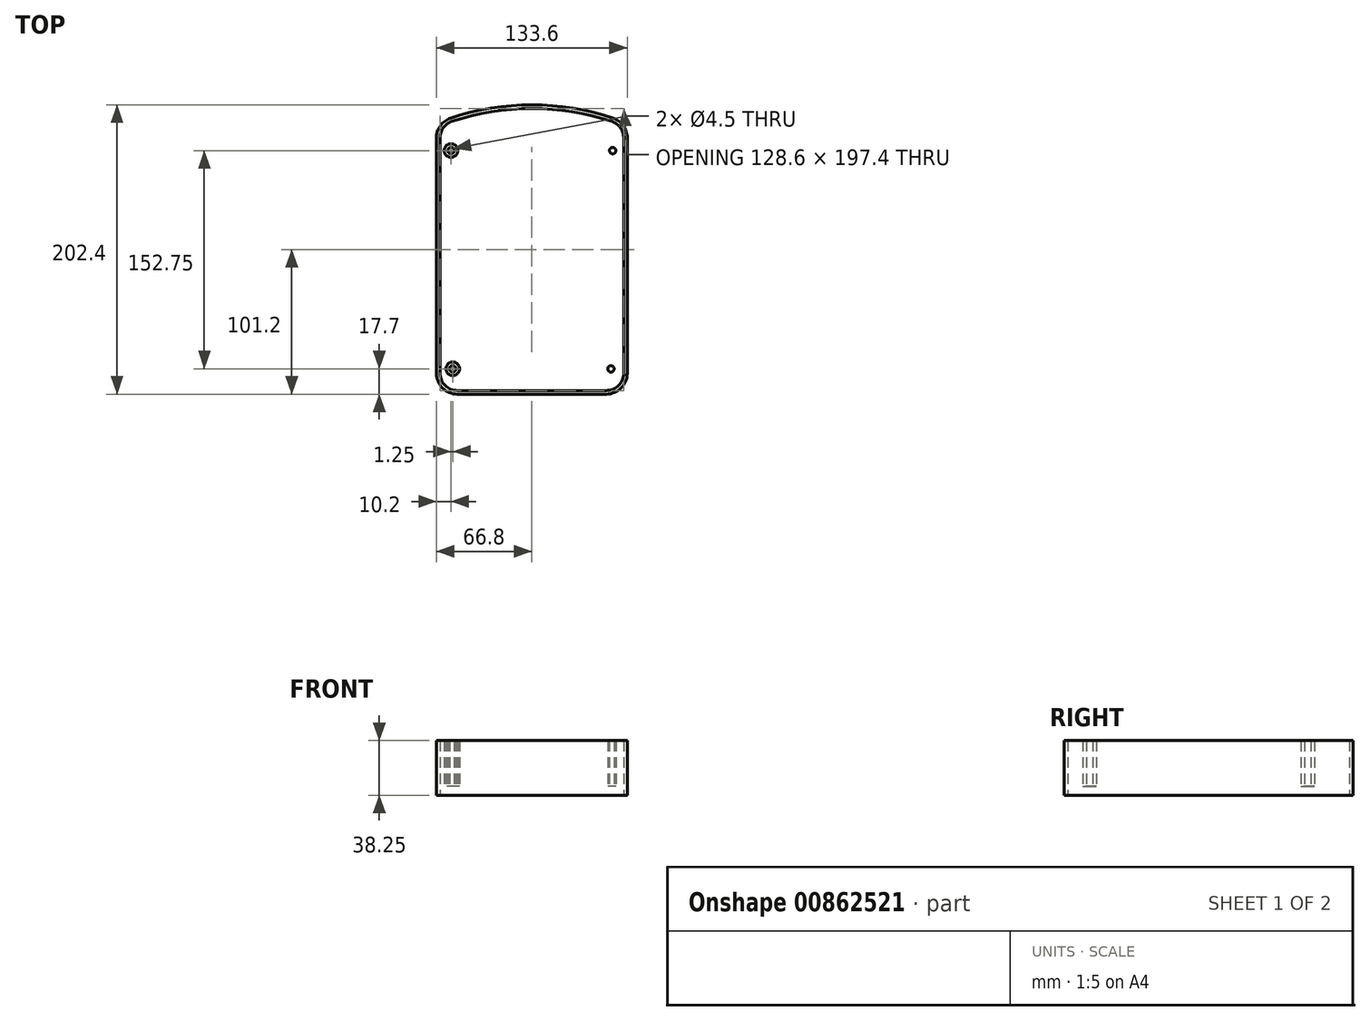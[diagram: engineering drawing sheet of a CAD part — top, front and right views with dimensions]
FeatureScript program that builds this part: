
annotation { "Feature Type Name" : "Feature", "Feature Type Description" : "" }
export const myFeature = defineFeature(function(context is Context, id is Id, definition is map)
    precondition{}
    {
        {
            var Q0;
            Q0=qCreatedBy(makeId("Top.planeOp"),FACE);
            var sketch = newSketch(context, id + "F0", { "sketchPlane" : qUnion([Q0])});
            skCircle(sketch, "E0", {"center": v(-55.35, -75) * mm, "radius": 2.25 * mm});
            skCircle(sketch, "E1", {"center": v(-56.6, 77.75) * mm, "radius": 2.25 * mm});
            skCircle(sketch, "E2.MirrorC", {"center": v(56.6, 77.75) * mm, "radius": 2.25 * mm});
            skCircle(sketch, "E3.MirrorC", {"center": v(55.35, -75) * mm, "radius": 2.25 * mm});
            skCircle(sketch, "E4", {"center": v(11.35, -59) * mm, "radius": 2.25 * mm});
            skLineSegment(sketch, "E5.bottom", {"start": v(-64.1, 95) * mm, "end": v(64.1, 95) * mm});
            skLineSegment(sketch, "E5.top", {"start": v(-52.1, -90) * mm, "end": v(52.1, -90) * mm});
            skLineSegment(sketch, "E5.left", {"start": v(-64.1, 86.57) * mm, "end": v(-64.1, -78) * mm});
            skLineSegment(sketch, "E5.right", {"start": v(64.1, 86.57) * mm, "end": v(64.1, -78) * mm});
            skPoint(sketch, "E5.middle", {"position": v(0, 2.5) * mm});
            skArc(sketch, "E6", {"start": v(55.88, 97.96) * mm, "mid": v(0, 107) * mm, "end": v(-55.88, 97.96) * mm});
            skPoint(sketch, "E7.visualSharp", {"position": v(-64.1, -90) * mm});
            skArc(sketch, "E7.filletArc", {"start": v(-64.1, -78) * mm, "mid": v(-60.59, -86.49) * mm, "end": v(-52.1, -90) * mm});
            skPoint(sketch, "E8.visualSharp", {"position": v(64.1, -90) * mm});
            skArc(sketch, "E8.filletArc", {"start": v(52.1, -90) * mm, "mid": v(60.59, -86.49) * mm, "end": v(64.1, -78) * mm});
            skPoint(sketch, "E9.visualSharp", {"position": v(-64.1, 95) * mm});
            skArc(sketch, "E9.filletArc", {"start": v(-55.88, 97.96) * mm, "mid": v(-61.83, 93.6) * mm, "end": v(-64.1, 86.57) * mm});
            skPoint(sketch, "E10.visualSharp", {"position": v(64.1, 95) * mm});
            skArc(sketch, "E10.filletArc", {"start": v(64.1, 86.57) * mm, "mid": v(61.83, 93.6) * mm, "end": v(55.88, 97.96) * mm});
            skCircle(sketch, "E11", {"center": v(56.6, 77.75) * mm, "radius": 4.75 * mm});
            skCircle(sketch, "E12", {"center": v(55.35, -75) * mm, "radius": 4.75 * mm});
            skCircle(sketch, "E13", {"center": v(-55.35, -75) * mm, "radius": 4.75 * mm});
            skCircle(sketch, "E14", {"center": v(-56.6, 77.75) * mm, "radius": 4.75 * mm});
            skLineSegment(sketch, "E15.0", {"start": v(-64.3, 86.57) * mm, "end": v(-64.3, -78) * mm});
            skLineSegment(sketch, "E16.0", {"start": v(64.3, 86.57) * mm, "end": v(64.3, -78) * mm});
            skArc(sketch, "E17.0", {"start": v(-64.3, -78) * mm, "mid": v(-60.73, -86.63) * mm, "end": v(-52.1, -90.2) * mm});
            skLineSegment(sketch, "E18.0", {"start": v(-52.1, -90.2) * mm, "end": v(52.1, -90.2) * mm});
            skArc(sketch, "E19.0", {"start": v(52.1, -90.2) * mm, "mid": v(60.73, -86.63) * mm, "end": v(64.3, -78) * mm});
            skArc(sketch, "E20.0", {"start": v(-55.95, 98.15) * mm, "mid": v(-62, 93.7) * mm, "end": v(-64.3, 86.57) * mm});
            skArc(sketch, "E21.0", {"start": v(55.95, 98.15) * mm, "mid": v(0, 107.2) * mm, "end": v(-55.95, 98.15) * mm});
            skArc(sketch, "E22.0", {"start": v(64.3, 86.57) * mm, "mid": v(62, 93.7) * mm, "end": v(55.95, 98.15) * mm});
            skArc(sketch, "E23.0", {"start": v(56.74, 100.52) * mm, "mid": v(0, 109.7) * mm, "end": v(-56.74, 100.52) * mm});
            skArc(sketch, "E24.0", {"start": v(-56.74, 100.52) * mm, "mid": v(-64.02, 95.17) * mm, "end": v(-66.8, 86.57) * mm});
            skLineSegment(sketch, "E25.0", {"start": v(-66.8, 86.57) * mm, "end": v(-66.8, -78) * mm});
            skArc(sketch, "E26.0", {"start": v(-66.8, -78) * mm, "mid": v(-62.5, -88.4) * mm, "end": v(-52.1, -92.7) * mm});
            skLineSegment(sketch, "E27.0", {"start": v(-52.1, -92.7) * mm, "end": v(52.1, -92.7) * mm});
            skArc(sketch, "E28.0", {"start": v(52.1, -92.7) * mm, "mid": v(62.5, -88.4) * mm, "end": v(66.8, -78) * mm});
            skLineSegment(sketch, "E29.0", {"start": v(66.8, 86.57) * mm, "end": v(66.8, -78) * mm});
            skArc(sketch, "E30.0", {"start": v(66.8, 86.57) * mm, "mid": v(64.02, 95.17) * mm, "end": v(56.74, 100.52) * mm});
            skSolve(sketch);
        }
        {
            var Q0;
            Q0=qCreatedBy(makeId("Top.planeOp"),FACE);
            cPlane(context, id + "F1", {"entities" : qUnion([Q0]), "cplaneType" : CPlaneType.OFFSET, "offset" : 32 * mm, "width" : 150 * mm, "height" : 150 * mm});
        }
        {
            var Q0;
            Q0=makeQuery(id+"F0.imprint","IMPRINT",FACE,{"disambiguationData":[TD([[makeQuery(id+"F0.imprint","IMPRINT",EDGE,{"derivedFrom":sQuery(id+"F0.wireOp",EDGE,"E1")}),-1.0]])]});
            var Q1;
            Q1=makeQuery(id+"F0.imprint","IMPRINT",FACE,{"disambiguationData":[TD([[makeQuery(id+"F0.imprint","IMPRINT",EDGE,{"derivedFrom":sQuery(id+"F0.wireOp",EDGE,"E2.MirrorC")}),1.0]])]});
            var Q2;
            Q2=makeQuery(id+"F0.imprint","IMPRINT",FACE,{"disambiguationData":[TD([[makeQuery(id+"F0.imprint","IMPRINT",EDGE,{"derivedFrom":sQuery(id+"F0.wireOp",EDGE,"E3.MirrorC")}),1.0]])]});
            var Q3;
            Q3=makeQuery(id+"F0.imprint","IMPRINT",FACE,{"disambiguationData":[TD([[makeQuery(id+"F0.imprint","IMPRINT",EDGE,{"derivedFrom":sQuery(id+"F0.wireOp",EDGE,"E0")}),-1.0]])]});
            var Q4;
            Q4=qCreatedBy(id+"F1.planeOp",FACE);
            extrude(context, id + "F2", {"entities" : qUnion([Q0, Q1, Q2, Q3]), "endBound" : BoundingType.UP_TO_SURFACE, "depth" : 25 * mm, "endBoundEntityFace" : qUnion([Q4]), "offsetDistance" : 25 * mm});
        }
        {
            var Q0;
            {var subQ6=sQuery(id+"F0.wireOp",EDGE,"E15.0");Q0=makeQuery(id+"F0.imprint","IMPRINT",FACE,{"disambiguationData":[TD([[makeQuery(id+"F0.imprint","IMPRINT",EDGE,{"derivedFrom":subQ6}),-1.0]])]});}
            var Q1;
            Q1=makeQuery(id+"F2.opExtrude","CAP_FACE",FACE,{"disambiguationData":[OSD([sQuery(id+"F0.wireOp",EDGE,"E1"),sQuery(id+"F0.wireOp",EDGE,"E14")])],"isStart":false});
            extrude(context, id + "F3", {"entities" : qUnion([Q0]), "endBound" : BoundingType.UP_TO_SURFACE, "depth" : 25 * mm, "endBoundEntityFace" : qUnion([Q1]), "offsetDistance" : 25 * mm, "hasSecondDirection" : true, "secondDirectionOppositeDirection" : true, "secondDirectionDepth" : 6.25 * mm});
        }
    });
